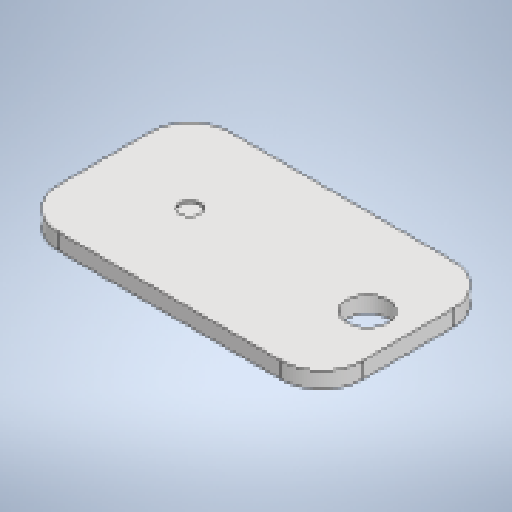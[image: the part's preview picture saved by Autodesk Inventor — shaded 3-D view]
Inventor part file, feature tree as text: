
AUTODESK INVENTOR PART (.ipt)
format: ipt  version: 2025.1 (Build 291241020, 241B)  size: 182,784 bytes
history: native  units: mm
features: sketch x2, other x2, sheet_metal_op x1, chamfer x1, extrude x1
ambient origin geometry x8: Origin, YZ Plane, XZ Plane, XY Plane, X Axis, Y Axis, Z Axis, Center Point
bodies: Solid1 (feature_tree)
feature tree (7):
  sheet_metal_op  "Face1"
  chamfer  "Corner Round1"
  extrude  "Extrusion2"  Depth=85.0mm
  sketch  "Sketch1"  dims[d0=150.0mm d1=85.0mm]
  other  "Plate1"
  sketch  "Sketch5"  dims[d2=8.0mm d22=5.0mm d23=20.0mm d25=20.0mm d26=20.0mm d27=10.0mm d28=1.0mm d29=0.0mm]
  other  "Definition1"
